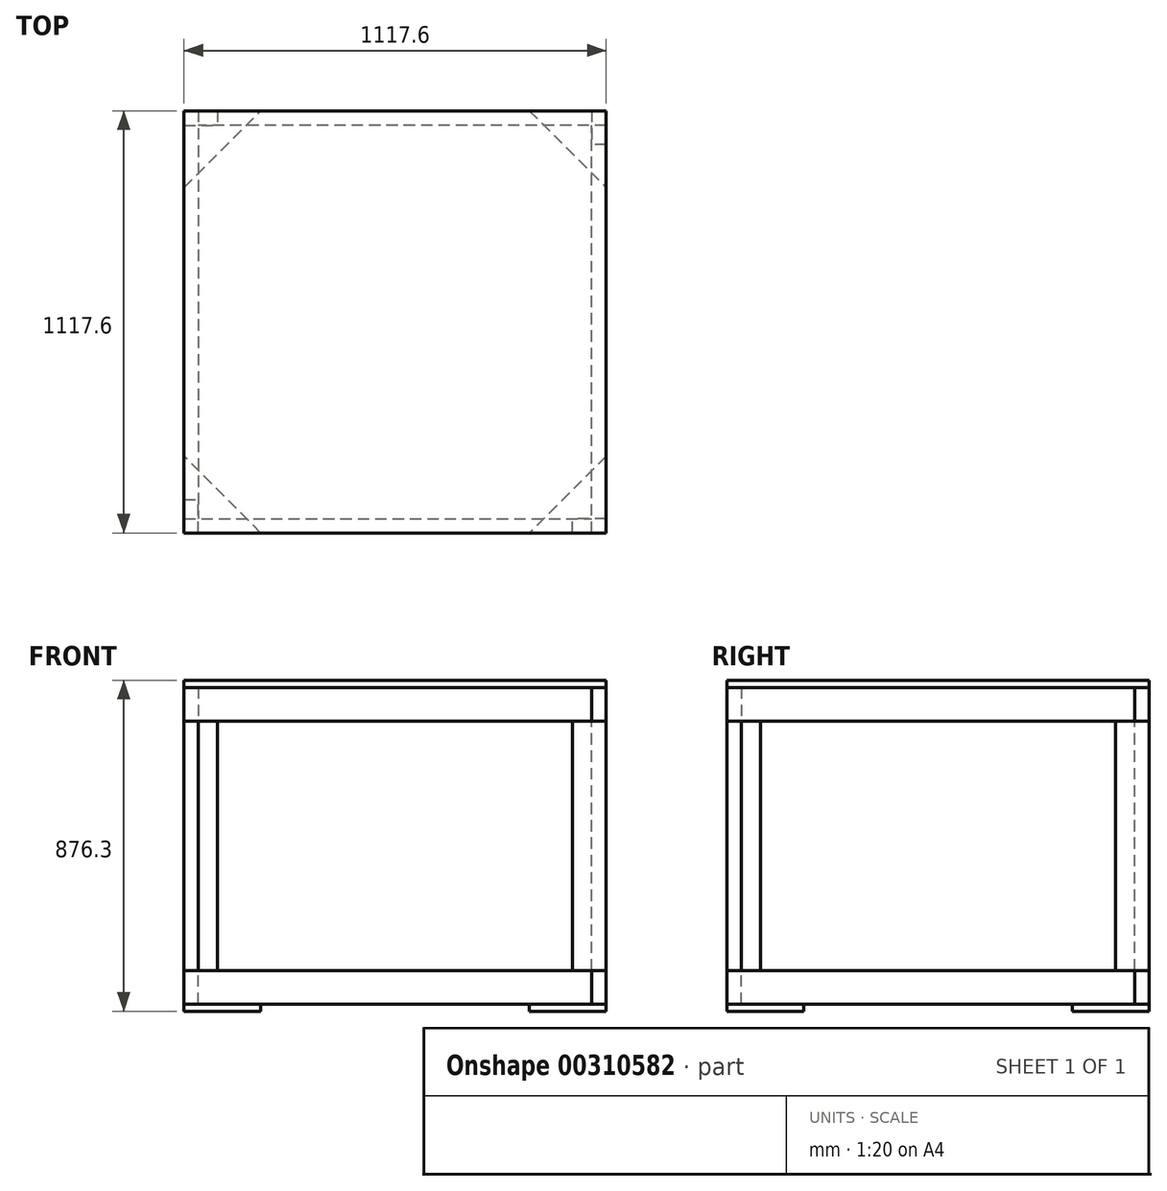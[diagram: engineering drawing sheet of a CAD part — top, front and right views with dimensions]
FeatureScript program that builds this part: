
annotation { "Feature Type Name" : "Feature", "Feature Type Description" : "" }
export const myFeature = defineFeature(function(context is Context, id is Id, definition is map)
    precondition{}
    {
        {
            var Q0;
            Q0=qCreatedBy(makeId("Top.planeOp"),FACE);
            var sketch = newSketch(context, id + "F0", { "sketchPlane" : qUnion([Q0])});
            skLineSegment(sketch, "E0.bottom", {"start": v(0, 0) * mm, "end": v(1117.6, 0) * mm, "construction": true});
            skLineSegment(sketch, "E0.top", {"start": v(0, 1117.6) * mm, "end": v(1117.6, 1117.6) * mm, "construction": true});
            skLineSegment(sketch, "E0.left", {"start": v(0, 0) * mm, "end": v(0, 1117.6) * mm, "construction": true});
            skLineSegment(sketch, "E0.right", {"start": v(1117.6, 0) * mm, "end": v(1117.6, 1117.6) * mm, "construction": true});
            skCircle(sketch, "E1", {"center": v(558.8, 558.8) * mm, "radius": 558.8 * mm, "construction": true});
            skLineSegment(sketch, "E2", {"start": v(0, 1117.6) * mm, "end": v(1117.6, 0) * mm, "construction": true});
            skLineSegment(sketch, "E3", {"start": v(1117.6, 1117.6) * mm, "end": v(0, 0) * mm, "construction": true});
            skSolve(sketch);
        }
        {
            var Q0;
            Q0=qCreatedBy(makeId("Top.planeOp"),FACE);
            var sketch = newSketch(context, id + "F1", { "sketchPlane" : qUnion([Q0])});
            skLineSegment(sketch, "E4.bottom", {"start": v(0, 1117.6) * mm, "end": v(38.1, 1117.6) * mm});
            skLineSegment(sketch, "E4.top", {"start": v(0, 38.1) * mm, "end": v(38.1, 38.1) * mm});
            skLineSegment(sketch, "E4.left", {"start": v(0, 1117.6) * mm, "end": v(0, 38.1) * mm});
            skLineSegment(sketch, "E4.right", {"start": v(38.1, 1117.6) * mm, "end": v(38.1, 38.1) * mm});
            skSolve(sketch);
        }
        {
            var Q0;
            Q0 = qSketchRegion(id + "F1", true);
            extrude(context, id + "F2", {"entities" : qUnion([Q0]), "depth" : 88.9 * mm});
        }
        {
            var Q0;
            Q0=makeQuery(id+"F2.opExtrude","SWEPT_BODY",BODY,{"disambiguationData":[OSD([sQuery(id+"F1.wireOp",EDGE,"E4.bottom"),sQuery(id+"F1.wireOp",EDGE,"E4.top"),sQuery(id+"F1.wireOp",EDGE,"E4.left"),sQuery(id+"F1.wireOp",EDGE,"E4.right")])]});
            var Q1;
            Q1=sQuery(id+"F0.wireOp",EDGE,"E1");
            circularPattern(context, id + "F3", {"entities" : qUnion([Q0]), "axis" : qUnion([Q1]), "angle" : 360 * degree, "instanceCount" : 4, "equalSpace" : true});
        }
        {
            var Q0;
            Q0=makeQuery(id+"F3.opPattern","COPY",FACE,{"derivedFrom":makeQuery(id+"F2.opExtrude","CAP_FACE",FACE,{"disambiguationData":[OSD([sQuery(id+"F1.wireOp",EDGE,"E4.bottom"),sQuery(id+"F1.wireOp",EDGE,"E4.top"),sQuery(id+"F1.wireOp",EDGE,"E4.left"),sQuery(id+"F1.wireOp",EDGE,"E4.right")])],"isStart":true}),"instanceName":"1"});
            cPlane(context, id + "F4", {"entities" : qUnion([Q0]), "cplaneType" : CPlaneType.OFFSET, "offset" : 330.2 * mm, "width" : 152.4 * mm, "height" : 152.4 * mm});
        }
        {
            var Q0;
            Q0=makeQuery(id+"F2.opExtrude","SWEPT_BODY",BODY,{"disambiguationData":[OSD([sQuery(id+"F1.wireOp",EDGE,"E4.bottom"),sQuery(id+"F1.wireOp",EDGE,"E4.top"),sQuery(id+"F1.wireOp",EDGE,"E4.left"),sQuery(id+"F1.wireOp",EDGE,"E4.right")])]});
            var Q1;
            Q1=makeQuery(id+"F3.opPattern","COPY",BODY,{"derivedFrom":makeQuery(id+"F2.opExtrude","SWEPT_BODY",BODY,{"disambiguationData":[OSD([sQuery(id+"F1.wireOp",EDGE,"E4.bottom"),sQuery(id+"F1.wireOp",EDGE,"E4.top"),sQuery(id+"F1.wireOp",EDGE,"E4.left"),sQuery(id+"F1.wireOp",EDGE,"E4.right")])]}),"instanceName":"1"});
            var Q2;
            Q2=makeQuery(id+"F3.opPattern","COPY",BODY,{"derivedFrom":makeQuery(id+"F2.opExtrude","SWEPT_BODY",BODY,{"disambiguationData":[OSD([sQuery(id+"F1.wireOp",EDGE,"E4.bottom"),sQuery(id+"F1.wireOp",EDGE,"E4.top"),sQuery(id+"F1.wireOp",EDGE,"E4.left"),sQuery(id+"F1.wireOp",EDGE,"E4.right")])]}),"instanceName":"2"});
            var Q3;
            Q3=makeQuery(id+"F3.opPattern","COPY",BODY,{"derivedFrom":makeQuery(id+"F2.opExtrude","SWEPT_BODY",BODY,{"disambiguationData":[OSD([sQuery(id+"F1.wireOp",EDGE,"E4.bottom"),sQuery(id+"F1.wireOp",EDGE,"E4.top"),sQuery(id+"F1.wireOp",EDGE,"E4.left"),sQuery(id+"F1.wireOp",EDGE,"E4.right")])]}),"instanceName":"3"});
            var Q4;
            Q4=qCreatedBy(id+"F4.planeOp",FACE);
            mirror(context, id + "F5", {"entities" : qUnion([Q0, Q1, Q2, Q3]), "mirrorPlane" : qUnion([Q4])});
        }
        {
            var Q0;
            Q0=makeQuery(id+"F3.opPattern","COPY",FACE,{"derivedFrom":makeQuery(id+"F2.opExtrude","CAP_FACE",FACE,{"disambiguationData":[OSD([sQuery(id+"F1.wireOp",EDGE,"E4.bottom"),sQuery(id+"F1.wireOp",EDGE,"E4.top"),sQuery(id+"F1.wireOp",EDGE,"E4.left"),sQuery(id+"F1.wireOp",EDGE,"E4.right")])],"isStart":true}),"instanceName":"1"});
            var sketch = newSketch(context, id + "F6", { "sketchPlane" : qUnion([Q0])});
            skLineSegment(sketch, "E5.bottom", {"start": v(0, 0) * mm, "end": v(38.1, 0) * mm});
            skLineSegment(sketch, "E5.top", {"start": v(0, -88.9) * mm, "end": v(38.1, -88.9) * mm});
            skLineSegment(sketch, "E5.left", {"start": v(0, 0) * mm, "end": v(0, -88.9) * mm});
            skLineSegment(sketch, "E5.right", {"start": v(38.1, 0) * mm, "end": v(38.1, -88.9) * mm});
            skSolve(sketch);
        }
        {
            var Q0;
            Q0 = qSketchRegion(id + "F6", true);
            var Q1;
            Q1=makeQuery(id+"F5.opPattern","COPY",FACE,{"derivedFrom":makeQuery(id+"F3.opPattern","COPY",FACE,{"derivedFrom":makeQuery(id+"F2.opExtrude","CAP_FACE",FACE,{"disambiguationData":[OSD([sQuery(id+"F1.wireOp",EDGE,"E4.bottom"),sQuery(id+"F1.wireOp",EDGE,"E4.top"),sQuery(id+"F1.wireOp",EDGE,"E4.left"),sQuery(id+"F1.wireOp",EDGE,"E4.right")])],"isStart":true}),"instanceName":"1"}),"instanceName":"1"});
            extrude(context, id + "F7", {"entities" : qUnion([Q0]), "endBound" : BoundingType.UP_TO_SURFACE, "endBoundEntityFace" : qUnion([Q1]), "depth" : 25.4 * mm});
        }
        {
            var Q0;
            Q0=makeQuery(id+"F7.opExtrude","SWEPT_BODY",BODY,{"disambiguationData":[OSD([sQuery(id+"F6.wireOp",EDGE,"E5.bottom"),sQuery(id+"F6.wireOp",EDGE,"E5.top"),sQuery(id+"F6.wireOp",EDGE,"E5.left"),sQuery(id+"F6.wireOp",EDGE,"E5.right")])]});
            var Q1;
            Q1=sQuery(id+"F0.wireOp",EDGE,"E1");
            circularPattern(context, id + "F8", {"entities" : qUnion([Q0]), "axis" : qUnion([Q1]), "angle" : 360 * degree, "instanceCount" : 4, "equalSpace" : true});
        }
        {
            var Q0;
            Q0=makeQuery(id+"F5.opPattern","COPY",FACE,{"derivedFrom":makeQuery(id+"F3.opPattern","COPY",FACE,{"derivedFrom":makeQuery(id+"F2.opExtrude","CAP_FACE",FACE,{"disambiguationData":[OSD([sQuery(id+"F1.wireOp",EDGE,"E4.bottom"),sQuery(id+"F1.wireOp",EDGE,"E4.top"),sQuery(id+"F1.wireOp",EDGE,"E4.left"),sQuery(id+"F1.wireOp",EDGE,"E4.right")])],"isStart":false}),"instanceName":"1"}),"instanceName":"1"});
            var sketch = newSketch(context, id + "F9", { "sketchPlane" : qUnion([Q0])});
            skLineSegment(sketch, "E6", {"start": v(0, 0) * mm, "end": v(203.2, 0) * mm});
            skLineSegment(sketch, "E7", {"start": v(203.2, 0) * mm, "end": v(0, -203.2) * mm});
            skLineSegment(sketch, "E8", {"start": v(0, -203.2) * mm, "end": v(0, 0) * mm});
            skSolve(sketch);
        }
        {
            var Q0;
            Q0 = qSketchRegion(id + "F9", true);
            extrude(context, id + "F10", {"entities" : qUnion([Q0]), "depth" : 19.05 * mm});
        }
        {
            var Q0;
            Q0=makeQuery(id+"F10.opExtrude","SWEPT_BODY",BODY,{"disambiguationData":[OSD([sQuery(id+"F9.wireOp",EDGE,"E6"),sQuery(id+"F9.wireOp",EDGE,"E7"),sQuery(id+"F9.wireOp",EDGE,"E8")])]});
            var Q1;
            Q1=sQuery(id+"F0.wireOp",EDGE,"E1");
            circularPattern(context, id + "F11", {"entities" : qUnion([Q0]), "axis" : qUnion([Q1]), "angle" : 360 * degree, "instanceCount" : 4, "equalSpace" : true});
        }
        {
            var Q0;
            Q0=makeQuery(id+"F2.opExtrude","CAP_FACE",FACE,{"disambiguationData":[OSD([sQuery(id+"F1.wireOp",EDGE,"E4.bottom"),sQuery(id+"F1.wireOp",EDGE,"E4.top"),sQuery(id+"F1.wireOp",EDGE,"E4.left"),sQuery(id+"F1.wireOp",EDGE,"E4.right")])],"isStart":false});
            var sketch = newSketch(context, id + "F12", { "sketchPlane" : qUnion([Q0])});
            skLineSegment(sketch, "E9.bottom", {"start": v(0, 1117.6) * mm, "end": v(1117.6, 1117.6) * mm});
            skLineSegment(sketch, "E9.top", {"start": v(0, 0) * mm, "end": v(1117.6, 0) * mm});
            skLineSegment(sketch, "E9.left", {"start": v(0, 1117.6) * mm, "end": v(0, 0) * mm});
            skLineSegment(sketch, "E9.right", {"start": v(1117.6, 1117.6) * mm, "end": v(1117.6, 0) * mm});
            skSolve(sketch);
        }
        {
            var Q0;
            Q0 = qSketchRegion(id + "F12", true);
            extrude(context, id + "F13", {"entities" : qUnion([Q0]), "depth" : 19.05 * mm});
        }
    });
